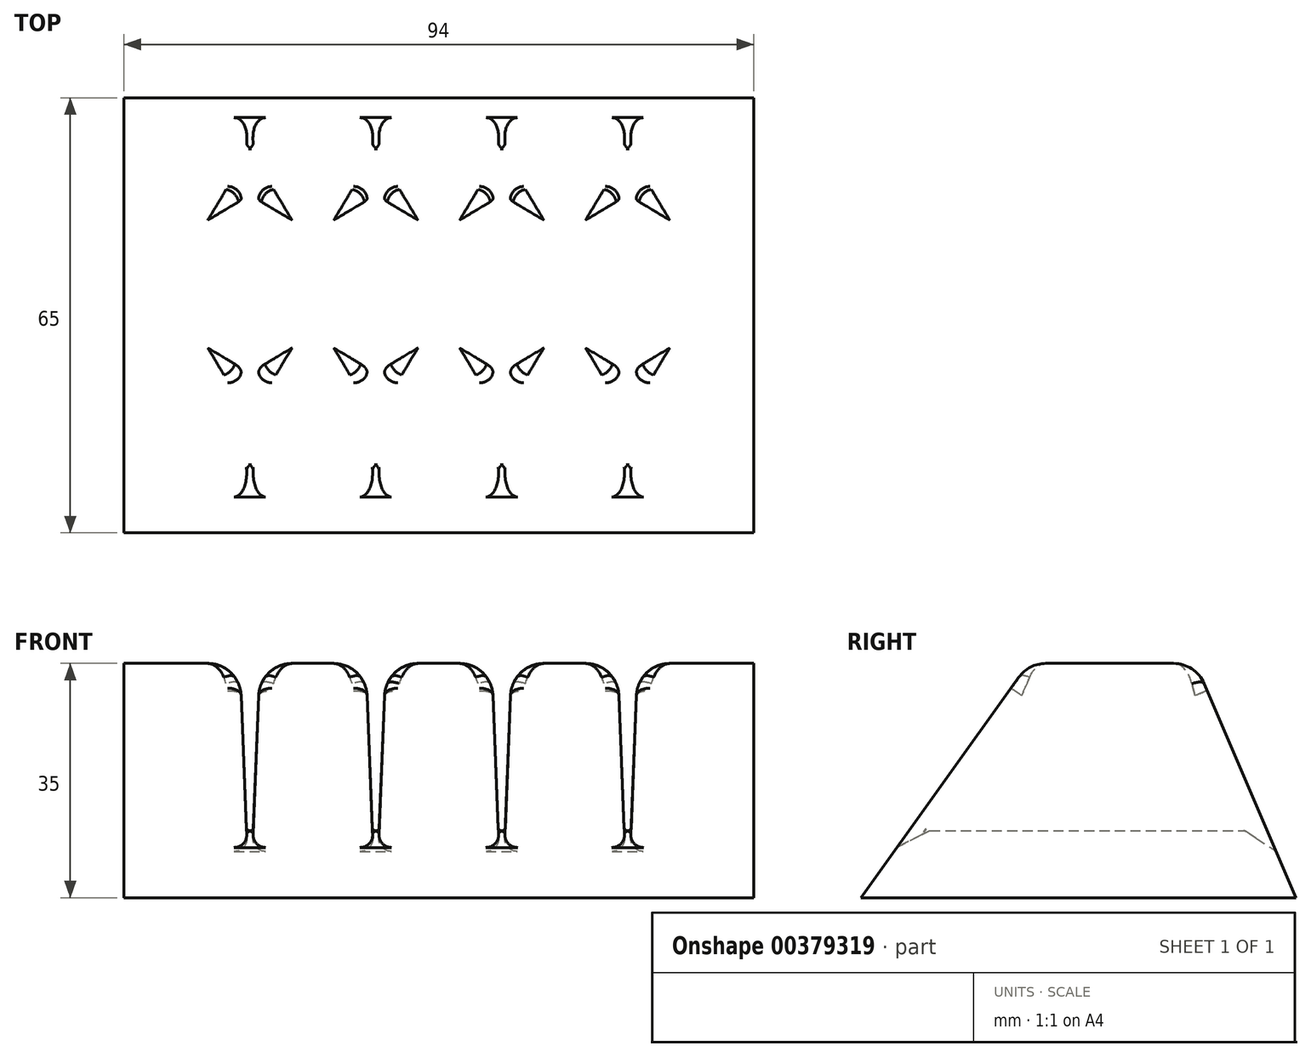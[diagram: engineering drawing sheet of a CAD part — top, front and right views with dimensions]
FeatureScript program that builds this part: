
annotation { "Feature Type Name" : "Feature", "Feature Type Description" : "" }
export const myFeature = defineFeature(function(context is Context, id is Id, definition is map)
    precondition{}
    {
        {
            var Q0;
            Q0=qCreatedBy(makeId("Front.planeOp"),FACE);
            var sketch = newSketch(context, id + "F0", { "sketchPlane" : qUnion([Q0])});
            skLineSegment(sketch, "E0", {"start": v(-114.12, 35) * mm, "end": v(-114.12, 0) * mm});
            skLineSegment(sketch, "E1", {"start": v(-114.12, 0) * mm, "end": v(-20.12, 0) * mm});
            skLineSegment(sketch, "E2", {"start": v(-20.12, 0) * mm, "end": v(-20.12, 35) * mm});
            skLineSegment(sketch, "E3", {"start": v(-56.22, 35) * mm, "end": v(-57.22, 10) * mm});
            skLineSegment(sketch, "E4", {"start": v(-57.22, 10) * mm, "end": v(-58.22, 10) * mm});
            skLineSegment(sketch, "E5", {"start": v(-58.22, 10) * mm, "end": v(-59.22, 35) * mm});
            skLineSegment(sketch, "E6", {"start": v(-75.02, 35) * mm, "end": v(-76.02, 10) * mm});
            skLineSegment(sketch, "E7", {"start": v(-76.02, 10) * mm, "end": v(-77.02, 10) * mm});
            skLineSegment(sketch, "E8", {"start": v(-77.02, 10) * mm, "end": v(-78.02, 35) * mm});
            skLineSegment(sketch, "E9", {"start": v(-93.82, 35) * mm, "end": v(-94.82, 10) * mm});
            skLineSegment(sketch, "E10", {"start": v(-94.82, 10) * mm, "end": v(-95.82, 10) * mm});
            skLineSegment(sketch, "E11", {"start": v(-95.82, 10) * mm, "end": v(-96.82, 35) * mm});
            skLineSegment(sketch, "E12", {"start": v(-38.42, 10) * mm, "end": v(-39.42, 10) * mm});
            skLineSegment(sketch, "E13", {"start": v(-39.42, 10) * mm, "end": v(-40.42, 35) * mm});
            skLineSegment(sketch, "E14", {"start": v(-37.42, 35) * mm, "end": v(-38.42, 10) * mm});
            skLineSegment(sketch, "E15", {"start": v(-114.12, 35) * mm, "end": v(-96.82, 35) * mm});
            skLineSegment(sketch, "E16", {"start": v(-93.82, 35) * mm, "end": v(-78.02, 35) * mm});
            skLineSegment(sketch, "E17", {"start": v(-75.02, 35) * mm, "end": v(-59.22, 35) * mm});
            skLineSegment(sketch, "E18", {"start": v(-56.22, 35) * mm, "end": v(-40.42, 35) * mm});
            skLineSegment(sketch, "E19", {"start": v(-37.42, 35) * mm, "end": v(-20.12, 35) * mm});
            skSolve(sketch);
        }
        {
            var Q0;
            Q0 = qSketchRegion(id + "F0", true);
            extrude(context, id + "F1", {"entities" : qUnion([Q0]), "depth" : 25 * mm});
        }
        {
            var Q0;
            Q0=makeQuery(id+"F1.opExtrude","CAP_FACE",FACE,{"disambiguationData":[OSD([sQuery(id+"F0.wireOp",EDGE,"E0"),sQuery(id+"F0.wireOp",EDGE,"E1"),sQuery(id+"F0.wireOp",EDGE,"E2"),sQuery(id+"F0.wireOp",EDGE,"E3"),sQuery(id+"F0.wireOp",EDGE,"E4"),sQuery(id+"F0.wireOp",EDGE,"E5"),sQuery(id+"F0.wireOp",EDGE,"E6"),sQuery(id+"F0.wireOp",EDGE,"E7"),sQuery(id+"F0.wireOp",EDGE,"E8"),sQuery(id+"F0.wireOp",EDGE,"E9"),sQuery(id+"F0.wireOp",EDGE,"E10"),sQuery(id+"F0.wireOp",EDGE,"E11"),sQuery(id+"F0.wireOp",EDGE,"E12"),sQuery(id+"F0.wireOp",EDGE,"E13"),sQuery(id+"F0.wireOp",EDGE,"E14"),sQuery(id+"F0.wireOp",EDGE,"E15"),sQuery(id+"F0.wireOp",EDGE,"E16"),sQuery(id+"F0.wireOp",EDGE,"E17"),sQuery(id+"F0.wireOp",EDGE,"E18"),sQuery(id+"F0.wireOp",EDGE,"E19")])],"isStart":false});
            extrude(context, id + "F2", {"entities" : qUnion([Q0]), "operationType" : NewBodyOperationType.ADD, "depth" : 25 * mm});
        }
        {
            var Q0;
            Q0=makeQuery(id+"F1.opExtrude","CAP_FACE",FACE,{"disambiguationData":[OSD([sQuery(id+"F0.wireOp",EDGE,"E0"),sQuery(id+"F0.wireOp",EDGE,"E1"),sQuery(id+"F0.wireOp",EDGE,"E2"),sQuery(id+"F0.wireOp",EDGE,"E3"),sQuery(id+"F0.wireOp",EDGE,"E4"),sQuery(id+"F0.wireOp",EDGE,"E5"),sQuery(id+"F0.wireOp",EDGE,"E6"),sQuery(id+"F0.wireOp",EDGE,"E7"),sQuery(id+"F0.wireOp",EDGE,"E8"),sQuery(id+"F0.wireOp",EDGE,"E9"),sQuery(id+"F0.wireOp",EDGE,"E10"),sQuery(id+"F0.wireOp",EDGE,"E11"),sQuery(id+"F0.wireOp",EDGE,"E12"),sQuery(id+"F0.wireOp",EDGE,"E13"),sQuery(id+"F0.wireOp",EDGE,"E14"),sQuery(id+"F0.wireOp",EDGE,"E15"),sQuery(id+"F0.wireOp",EDGE,"E16"),sQuery(id+"F0.wireOp",EDGE,"E17"),sQuery(id+"F0.wireOp",EDGE,"E18"),sQuery(id+"F0.wireOp",EDGE,"E19")])],"isStart":true});
            extrude(context, id + "F3", {"entities" : qUnion([Q0]), "operationType" : NewBodyOperationType.ADD, "depth" : 15 * mm});
        }
        {
            var Q0;
            {var subQ0=sQuery(id+"F0.wireOp",EDGE,"E0");Q0=makeQuery(id+"F3.boolean.opBoolean","MERGE",FACE,{"derivedFrom":[makeQuery(id+"F2.boolean.opBoolean","MERGE",FACE,{"derivedFrom":[makeQuery(id+"F1.opExtrude","SWEPT_FACE",FACE,{"disambiguationData":[OSD([subQ0])]}),makeQuery(id+"F2.opExtrude","SWEPT_FACE",FACE,{"disambiguationData":[OSD([subQ0])]})]}),makeQuery(id+"F3.opExtrude","SWEPT_FACE",FACE,{"disambiguationData":[OSD([subQ0])]})]});}
            var sketch = newSketch(context, id + "F4", { "sketchPlane" : qUnion([Q0])});
            skLineSegment(sketch, "E20", {"start": v(24.92, 35) * mm, "end": v(50, 0) * mm});
            skLineSegment(sketch, "E21", {"start": v(50, 0) * mm, "end": v(68.12, 0) * mm});
            skLineSegment(sketch, "E22", {"start": v(68.12, 0) * mm, "end": v(68.12, 46.5) * mm});
            skLineSegment(sketch, "E23", {"start": v(68.12, 46.5) * mm, "end": v(24.92, 35) * mm});
            skSolve(sketch);
        }
        {
            var Q0;
            Q0 = qSketchRegion(id + "F4", true);
            extrude(context, id + "F5", {"entities" : qUnion([Q0]), "operationType" : NewBodyOperationType.REMOVE, "endBound" : BoundingType.THROUGH_ALL, "oppositeDirection" : true, "depth" : 25 * mm});
        }
        {
            var Q0;
            {var subQ0=sQuery(id+"F0.wireOp",EDGE,"E0");Q0=makeQuery(id+"F3.boolean.opBoolean","MERGE",FACE,{"derivedFrom":[makeQuery(id+"F2.boolean.opBoolean","MERGE",FACE,{"derivedFrom":[makeQuery(id+"F1.opExtrude","SWEPT_FACE",FACE,{"disambiguationData":[OSD([subQ0])]}),makeQuery(id+"F2.opExtrude","SWEPT_FACE",FACE,{"disambiguationData":[OSD([subQ0])]})]}),makeQuery(id+"F3.opExtrude","SWEPT_FACE",FACE,{"disambiguationData":[OSD([subQ0])]})]});}
            var sketch = newSketch(context, id + "F6", { "sketchPlane" : qUnion([Q0])});
            skLineSegment(sketch, "E24", {"start": v(0, 35) * mm, "end": v(-15, 0) * mm});
            skLineSegment(sketch, "E25", {"start": v(-15, 0) * mm, "end": v(-37.92, 17) * mm});
            skLineSegment(sketch, "E26", {"start": v(-37.92, 17) * mm, "end": v(-15.46, 39.89) * mm});
            skLineSegment(sketch, "E27", {"start": v(-15.46, 39.89) * mm, "end": v(0, 35) * mm});
            skSolve(sketch);
        }
        {
            var Q0;
            Q0 = qSketchRegion(id + "F6", true);
            extrude(context, id + "F7", {"entities" : qUnion([Q0]), "operationType" : NewBodyOperationType.REMOVE, "endBound" : BoundingType.THROUGH_ALL, "oppositeDirection" : true, "depth" : 25 * mm});
        }
        {
            var Q0;
            {var subQ0=sQuery(id+"F0.wireOp",EDGE,"E14");Q0=makeQuery(id+"F7.boolean.opBoolean","INTERSECT",EDGE,{"derivedFrom":[makeQuery(id+"F3.boolean.opBoolean","MERGE",FACE,{"derivedFrom":[makeQuery(id+"F2.boolean.opBoolean","MERGE",FACE,{"derivedFrom":[makeQuery(id+"F1.opExtrude","SWEPT_FACE",FACE,{"disambiguationData":[OSD([subQ0])]}),makeQuery(id+"F2.opExtrude","SWEPT_FACE",FACE,{"disambiguationData":[OSD([subQ0])]})]}),makeQuery(id+"F3.opExtrude","SWEPT_FACE",FACE,{"disambiguationData":[OSD([subQ0])]})]}),makeQuery(id+"F7.opExtrude","SWEPT_FACE",FACE,{"disambiguationData":[OSD([sQuery(id+"F6.wireOp",EDGE,"E24")])]})]});}
            var Q1;
            {var subQ0=sQuery(id+"F0.wireOp",EDGE,"E13");Q1=makeQuery(id+"F7.boolean.opBoolean","INTERSECT",EDGE,{"derivedFrom":[makeQuery(id+"F3.boolean.opBoolean","MERGE",FACE,{"derivedFrom":[makeQuery(id+"F2.boolean.opBoolean","MERGE",FACE,{"derivedFrom":[makeQuery(id+"F1.opExtrude","SWEPT_FACE",FACE,{"disambiguationData":[OSD([subQ0])]}),makeQuery(id+"F2.opExtrude","SWEPT_FACE",FACE,{"disambiguationData":[OSD([subQ0])]})]}),makeQuery(id+"F3.opExtrude","SWEPT_FACE",FACE,{"disambiguationData":[OSD([subQ0])]})]}),makeQuery(id+"F7.opExtrude","SWEPT_FACE",FACE,{"disambiguationData":[OSD([sQuery(id+"F6.wireOp",EDGE,"E24")])]})]});}
            var Q2;
            {var subQ0=sQuery(id+"F0.wireOp",EDGE,"E3");Q2=makeQuery(id+"F7.boolean.opBoolean","INTERSECT",EDGE,{"derivedFrom":[makeQuery(id+"F3.boolean.opBoolean","MERGE",FACE,{"derivedFrom":[makeQuery(id+"F2.boolean.opBoolean","MERGE",FACE,{"derivedFrom":[makeQuery(id+"F1.opExtrude","SWEPT_FACE",FACE,{"disambiguationData":[OSD([subQ0])]}),makeQuery(id+"F2.opExtrude","SWEPT_FACE",FACE,{"disambiguationData":[OSD([subQ0])]})]}),makeQuery(id+"F3.opExtrude","SWEPT_FACE",FACE,{"disambiguationData":[OSD([subQ0])]})]}),makeQuery(id+"F7.opExtrude","SWEPT_FACE",FACE,{"disambiguationData":[OSD([sQuery(id+"F6.wireOp",EDGE,"E24")])]})]});}
            var Q3;
            {var subQ0=sQuery(id+"F0.wireOp",EDGE,"E5");Q3=makeQuery(id+"F7.boolean.opBoolean","INTERSECT",EDGE,{"derivedFrom":[makeQuery(id+"F3.boolean.opBoolean","MERGE",FACE,{"derivedFrom":[makeQuery(id+"F2.boolean.opBoolean","MERGE",FACE,{"derivedFrom":[makeQuery(id+"F1.opExtrude","SWEPT_FACE",FACE,{"disambiguationData":[OSD([subQ0])]}),makeQuery(id+"F2.opExtrude","SWEPT_FACE",FACE,{"disambiguationData":[OSD([subQ0])]})]}),makeQuery(id+"F3.opExtrude","SWEPT_FACE",FACE,{"disambiguationData":[OSD([subQ0])]})]}),makeQuery(id+"F7.opExtrude","SWEPT_FACE",FACE,{"disambiguationData":[OSD([sQuery(id+"F6.wireOp",EDGE,"E24")])]})]});}
            var Q4;
            {var subQ0=sQuery(id+"F0.wireOp",EDGE,"E6");Q4=makeQuery(id+"F7.boolean.opBoolean","INTERSECT",EDGE,{"derivedFrom":[makeQuery(id+"F3.boolean.opBoolean","MERGE",FACE,{"derivedFrom":[makeQuery(id+"F2.boolean.opBoolean","MERGE",FACE,{"derivedFrom":[makeQuery(id+"F1.opExtrude","SWEPT_FACE",FACE,{"disambiguationData":[OSD([subQ0])]}),makeQuery(id+"F2.opExtrude","SWEPT_FACE",FACE,{"disambiguationData":[OSD([subQ0])]})]}),makeQuery(id+"F3.opExtrude","SWEPT_FACE",FACE,{"disambiguationData":[OSD([subQ0])]})]}),makeQuery(id+"F7.opExtrude","SWEPT_FACE",FACE,{"disambiguationData":[OSD([sQuery(id+"F6.wireOp",EDGE,"E24")])]})]});}
            var Q5;
            {var subQ0=sQuery(id+"F0.wireOp",EDGE,"E8");Q5=makeQuery(id+"F7.boolean.opBoolean","INTERSECT",EDGE,{"derivedFrom":[makeQuery(id+"F3.boolean.opBoolean","MERGE",FACE,{"derivedFrom":[makeQuery(id+"F2.boolean.opBoolean","MERGE",FACE,{"derivedFrom":[makeQuery(id+"F1.opExtrude","SWEPT_FACE",FACE,{"disambiguationData":[OSD([subQ0])]}),makeQuery(id+"F2.opExtrude","SWEPT_FACE",FACE,{"disambiguationData":[OSD([subQ0])]})]}),makeQuery(id+"F3.opExtrude","SWEPT_FACE",FACE,{"disambiguationData":[OSD([subQ0])]})]}),makeQuery(id+"F7.opExtrude","SWEPT_FACE",FACE,{"disambiguationData":[OSD([sQuery(id+"F6.wireOp",EDGE,"E24")])]})]});}
            var Q6;
            {var subQ0=sQuery(id+"F0.wireOp",EDGE,"E9");Q6=makeQuery(id+"F7.boolean.opBoolean","INTERSECT",EDGE,{"derivedFrom":[makeQuery(id+"F3.boolean.opBoolean","MERGE",FACE,{"derivedFrom":[makeQuery(id+"F2.boolean.opBoolean","MERGE",FACE,{"derivedFrom":[makeQuery(id+"F1.opExtrude","SWEPT_FACE",FACE,{"disambiguationData":[OSD([subQ0])]}),makeQuery(id+"F2.opExtrude","SWEPT_FACE",FACE,{"disambiguationData":[OSD([subQ0])]})]}),makeQuery(id+"F3.opExtrude","SWEPT_FACE",FACE,{"disambiguationData":[OSD([subQ0])]})]}),makeQuery(id+"F7.opExtrude","SWEPT_FACE",FACE,{"disambiguationData":[OSD([sQuery(id+"F6.wireOp",EDGE,"E24")])]})]});}
            var Q7;
            {var subQ0=sQuery(id+"F0.wireOp",EDGE,"E11");Q7=makeQuery(id+"F7.boolean.opBoolean","INTERSECT",EDGE,{"derivedFrom":[makeQuery(id+"F3.boolean.opBoolean","MERGE",FACE,{"derivedFrom":[makeQuery(id+"F2.boolean.opBoolean","MERGE",FACE,{"derivedFrom":[makeQuery(id+"F1.opExtrude","SWEPT_FACE",FACE,{"disambiguationData":[OSD([subQ0])]}),makeQuery(id+"F2.opExtrude","SWEPT_FACE",FACE,{"disambiguationData":[OSD([subQ0])]})]}),makeQuery(id+"F3.opExtrude","SWEPT_FACE",FACE,{"disambiguationData":[OSD([subQ0])]})]}),makeQuery(id+"F7.opExtrude","SWEPT_FACE",FACE,{"disambiguationData":[OSD([sQuery(id+"F6.wireOp",EDGE,"E24")])]})]});}
            var Q8;
            {var subQ0=sQuery(id+"F0.wireOp",EDGE,"E11");Q8=makeQuery(id+"F5.boolean.opBoolean","INTERSECT",EDGE,{"derivedFrom":[makeQuery(id+"F3.boolean.opBoolean","MERGE",FACE,{"derivedFrom":[makeQuery(id+"F2.boolean.opBoolean","MERGE",FACE,{"derivedFrom":[makeQuery(id+"F1.opExtrude","SWEPT_FACE",FACE,{"disambiguationData":[OSD([subQ0])]}),makeQuery(id+"F2.opExtrude","SWEPT_FACE",FACE,{"disambiguationData":[OSD([subQ0])]})]}),makeQuery(id+"F3.opExtrude","SWEPT_FACE",FACE,{"disambiguationData":[OSD([subQ0])]})]}),makeQuery(id+"F5.opExtrude","SWEPT_FACE",FACE,{"disambiguationData":[OSD([sQuery(id+"F4.wireOp",EDGE,"E20")])]})]});}
            var Q9;
            {var subQ0=sQuery(id+"F0.wireOp",EDGE,"E9");Q9=makeQuery(id+"F5.boolean.opBoolean","INTERSECT",EDGE,{"derivedFrom":[makeQuery(id+"F3.boolean.opBoolean","MERGE",FACE,{"derivedFrom":[makeQuery(id+"F2.boolean.opBoolean","MERGE",FACE,{"derivedFrom":[makeQuery(id+"F1.opExtrude","SWEPT_FACE",FACE,{"disambiguationData":[OSD([subQ0])]}),makeQuery(id+"F2.opExtrude","SWEPT_FACE",FACE,{"disambiguationData":[OSD([subQ0])]})]}),makeQuery(id+"F3.opExtrude","SWEPT_FACE",FACE,{"disambiguationData":[OSD([subQ0])]})]}),makeQuery(id+"F5.opExtrude","SWEPT_FACE",FACE,{"disambiguationData":[OSD([sQuery(id+"F4.wireOp",EDGE,"E20")])]})]});}
            var Q10;
            {var subQ0=sQuery(id+"F0.wireOp",EDGE,"E8");Q10=makeQuery(id+"F5.boolean.opBoolean","INTERSECT",EDGE,{"derivedFrom":[makeQuery(id+"F3.boolean.opBoolean","MERGE",FACE,{"derivedFrom":[makeQuery(id+"F2.boolean.opBoolean","MERGE",FACE,{"derivedFrom":[makeQuery(id+"F1.opExtrude","SWEPT_FACE",FACE,{"disambiguationData":[OSD([subQ0])]}),makeQuery(id+"F2.opExtrude","SWEPT_FACE",FACE,{"disambiguationData":[OSD([subQ0])]})]}),makeQuery(id+"F3.opExtrude","SWEPT_FACE",FACE,{"disambiguationData":[OSD([subQ0])]})]}),makeQuery(id+"F5.opExtrude","SWEPT_FACE",FACE,{"disambiguationData":[OSD([sQuery(id+"F4.wireOp",EDGE,"E20")])]})]});}
            var Q11;
            {var subQ0=sQuery(id+"F0.wireOp",EDGE,"E6");Q11=makeQuery(id+"F5.boolean.opBoolean","INTERSECT",EDGE,{"derivedFrom":[makeQuery(id+"F3.boolean.opBoolean","MERGE",FACE,{"derivedFrom":[makeQuery(id+"F2.boolean.opBoolean","MERGE",FACE,{"derivedFrom":[makeQuery(id+"F1.opExtrude","SWEPT_FACE",FACE,{"disambiguationData":[OSD([subQ0])]}),makeQuery(id+"F2.opExtrude","SWEPT_FACE",FACE,{"disambiguationData":[OSD([subQ0])]})]}),makeQuery(id+"F3.opExtrude","SWEPT_FACE",FACE,{"disambiguationData":[OSD([subQ0])]})]}),makeQuery(id+"F5.opExtrude","SWEPT_FACE",FACE,{"disambiguationData":[OSD([sQuery(id+"F4.wireOp",EDGE,"E20")])]})]});}
            var Q12;
            {var subQ0=sQuery(id+"F0.wireOp",EDGE,"E5");Q12=makeQuery(id+"F5.boolean.opBoolean","INTERSECT",EDGE,{"derivedFrom":[makeQuery(id+"F3.boolean.opBoolean","MERGE",FACE,{"derivedFrom":[makeQuery(id+"F2.boolean.opBoolean","MERGE",FACE,{"derivedFrom":[makeQuery(id+"F1.opExtrude","SWEPT_FACE",FACE,{"disambiguationData":[OSD([subQ0])]}),makeQuery(id+"F2.opExtrude","SWEPT_FACE",FACE,{"disambiguationData":[OSD([subQ0])]})]}),makeQuery(id+"F3.opExtrude","SWEPT_FACE",FACE,{"disambiguationData":[OSD([subQ0])]})]}),makeQuery(id+"F5.opExtrude","SWEPT_FACE",FACE,{"disambiguationData":[OSD([sQuery(id+"F4.wireOp",EDGE,"E20")])]})]});}
            var Q13;
            {var subQ0=sQuery(id+"F0.wireOp",EDGE,"E3");Q13=makeQuery(id+"F5.boolean.opBoolean","INTERSECT",EDGE,{"derivedFrom":[makeQuery(id+"F3.boolean.opBoolean","MERGE",FACE,{"derivedFrom":[makeQuery(id+"F2.boolean.opBoolean","MERGE",FACE,{"derivedFrom":[makeQuery(id+"F1.opExtrude","SWEPT_FACE",FACE,{"disambiguationData":[OSD([subQ0])]}),makeQuery(id+"F2.opExtrude","SWEPT_FACE",FACE,{"disambiguationData":[OSD([subQ0])]})]}),makeQuery(id+"F3.opExtrude","SWEPT_FACE",FACE,{"disambiguationData":[OSD([subQ0])]})]}),makeQuery(id+"F5.opExtrude","SWEPT_FACE",FACE,{"disambiguationData":[OSD([sQuery(id+"F4.wireOp",EDGE,"E20")])]})]});}
            var Q14;
            {var subQ0=sQuery(id+"F0.wireOp",EDGE,"E13");Q14=makeQuery(id+"F5.boolean.opBoolean","INTERSECT",EDGE,{"derivedFrom":[makeQuery(id+"F3.boolean.opBoolean","MERGE",FACE,{"derivedFrom":[makeQuery(id+"F2.boolean.opBoolean","MERGE",FACE,{"derivedFrom":[makeQuery(id+"F1.opExtrude","SWEPT_FACE",FACE,{"disambiguationData":[OSD([subQ0])]}),makeQuery(id+"F2.opExtrude","SWEPT_FACE",FACE,{"disambiguationData":[OSD([subQ0])]})]}),makeQuery(id+"F3.opExtrude","SWEPT_FACE",FACE,{"disambiguationData":[OSD([subQ0])]})]}),makeQuery(id+"F5.opExtrude","SWEPT_FACE",FACE,{"disambiguationData":[OSD([sQuery(id+"F4.wireOp",EDGE,"E20")])]})]});}
            var Q15;
            {var subQ0=sQuery(id+"F0.wireOp",EDGE,"E14");Q15=makeQuery(id+"F5.boolean.opBoolean","INTERSECT",EDGE,{"derivedFrom":[makeQuery(id+"F3.boolean.opBoolean","MERGE",FACE,{"derivedFrom":[makeQuery(id+"F2.boolean.opBoolean","MERGE",FACE,{"derivedFrom":[makeQuery(id+"F1.opExtrude","SWEPT_FACE",FACE,{"disambiguationData":[OSD([subQ0])]}),makeQuery(id+"F2.opExtrude","SWEPT_FACE",FACE,{"disambiguationData":[OSD([subQ0])]})]}),makeQuery(id+"F3.opExtrude","SWEPT_FACE",FACE,{"disambiguationData":[OSD([subQ0])]})]}),makeQuery(id+"F5.opExtrude","SWEPT_FACE",FACE,{"disambiguationData":[OSD([sQuery(id+"F4.wireOp",EDGE,"E20")])]})]});}
            fillet(context, id + "F8", {"entities" : qUnion([Q0, Q1, Q2, Q3, Q4, Q5, Q6, Q7, Q8, Q9, Q10, Q11, Q12, Q13, Q14, Q15]), "radius" : 2 * mm, "tangentPropagation" : true, "allowEdgeOverflow" : false});
        }
        {
            var Q0;
            {var subQ0=sQuery(id+"F0.wireOp",EDGE,"E10");Q0=makeQuery(id+"F5.boolean.opBoolean","INTERSECT",EDGE,{"derivedFrom":[makeQuery(id+"F3.boolean.opBoolean","MERGE",FACE,{"derivedFrom":[makeQuery(id+"F2.boolean.opBoolean","MERGE",FACE,{"derivedFrom":[makeQuery(id+"F1.opExtrude","SWEPT_FACE",FACE,{"disambiguationData":[OSD([subQ0])]}),makeQuery(id+"F2.opExtrude","SWEPT_FACE",FACE,{"disambiguationData":[OSD([subQ0])]})]}),makeQuery(id+"F3.opExtrude","SWEPT_FACE",FACE,{"disambiguationData":[OSD([subQ0])]})]}),makeQuery(id+"F5.opExtrude","SWEPT_FACE",FACE,{"disambiguationData":[OSD([sQuery(id+"F4.wireOp",EDGE,"E20")])]})]});}
            var Q1;
            {var subQ0=sQuery(id+"F0.wireOp",EDGE,"E7");Q1=makeQuery(id+"F5.boolean.opBoolean","INTERSECT",EDGE,{"derivedFrom":[makeQuery(id+"F3.boolean.opBoolean","MERGE",FACE,{"derivedFrom":[makeQuery(id+"F2.boolean.opBoolean","MERGE",FACE,{"derivedFrom":[makeQuery(id+"F1.opExtrude","SWEPT_FACE",FACE,{"disambiguationData":[OSD([subQ0])]}),makeQuery(id+"F2.opExtrude","SWEPT_FACE",FACE,{"disambiguationData":[OSD([subQ0])]})]}),makeQuery(id+"F3.opExtrude","SWEPT_FACE",FACE,{"disambiguationData":[OSD([subQ0])]})]}),makeQuery(id+"F5.opExtrude","SWEPT_FACE",FACE,{"disambiguationData":[OSD([sQuery(id+"F4.wireOp",EDGE,"E20")])]})]});}
            var Q2;
            {var subQ0=sQuery(id+"F0.wireOp",EDGE,"E4");Q2=makeQuery(id+"F5.boolean.opBoolean","INTERSECT",EDGE,{"derivedFrom":[makeQuery(id+"F3.boolean.opBoolean","MERGE",FACE,{"derivedFrom":[makeQuery(id+"F2.boolean.opBoolean","MERGE",FACE,{"derivedFrom":[makeQuery(id+"F1.opExtrude","SWEPT_FACE",FACE,{"disambiguationData":[OSD([subQ0])]}),makeQuery(id+"F2.opExtrude","SWEPT_FACE",FACE,{"disambiguationData":[OSD([subQ0])]})]}),makeQuery(id+"F3.opExtrude","SWEPT_FACE",FACE,{"disambiguationData":[OSD([subQ0])]})]}),makeQuery(id+"F5.opExtrude","SWEPT_FACE",FACE,{"disambiguationData":[OSD([sQuery(id+"F4.wireOp",EDGE,"E20")])]})]});}
            var Q3;
            {var subQ0=sQuery(id+"F0.wireOp",EDGE,"E12");Q3=makeQuery(id+"F5.boolean.opBoolean","INTERSECT",EDGE,{"derivedFrom":[makeQuery(id+"F3.boolean.opBoolean","MERGE",FACE,{"derivedFrom":[makeQuery(id+"F2.boolean.opBoolean","MERGE",FACE,{"derivedFrom":[makeQuery(id+"F1.opExtrude","SWEPT_FACE",FACE,{"disambiguationData":[OSD([subQ0])]}),makeQuery(id+"F2.opExtrude","SWEPT_FACE",FACE,{"disambiguationData":[OSD([subQ0])]})]}),makeQuery(id+"F3.opExtrude","SWEPT_FACE",FACE,{"disambiguationData":[OSD([subQ0])]})]}),makeQuery(id+"F5.opExtrude","SWEPT_FACE",FACE,{"disambiguationData":[OSD([sQuery(id+"F4.wireOp",EDGE,"E20")])]})]});}
            chamfer(context, id + "F9", {"entities" : qUnion([Q0, Q1, Q2, Q3]), "width" : 6 * mm, "tangentPropagation" : true});
        }
        {
            var Q0;
            {var subQ0=sQuery(id+"F0.wireOp",EDGE,"E12");Q0=makeQuery(id+"F7.boolean.opBoolean","INTERSECT",EDGE,{"derivedFrom":[makeQuery(id+"F3.boolean.opBoolean","MERGE",FACE,{"derivedFrom":[makeQuery(id+"F2.boolean.opBoolean","MERGE",FACE,{"derivedFrom":[makeQuery(id+"F1.opExtrude","SWEPT_FACE",FACE,{"disambiguationData":[OSD([subQ0])]}),makeQuery(id+"F2.opExtrude","SWEPT_FACE",FACE,{"disambiguationData":[OSD([subQ0])]})]}),makeQuery(id+"F3.opExtrude","SWEPT_FACE",FACE,{"disambiguationData":[OSD([subQ0])]})]}),makeQuery(id+"F7.opExtrude","SWEPT_FACE",FACE,{"disambiguationData":[OSD([sQuery(id+"F6.wireOp",EDGE,"E24")])]})]});}
            var Q1;
            {var subQ0=sQuery(id+"F0.wireOp",EDGE,"E4");Q1=makeQuery(id+"F7.boolean.opBoolean","INTERSECT",EDGE,{"derivedFrom":[makeQuery(id+"F3.boolean.opBoolean","MERGE",FACE,{"derivedFrom":[makeQuery(id+"F2.boolean.opBoolean","MERGE",FACE,{"derivedFrom":[makeQuery(id+"F1.opExtrude","SWEPT_FACE",FACE,{"disambiguationData":[OSD([subQ0])]}),makeQuery(id+"F2.opExtrude","SWEPT_FACE",FACE,{"disambiguationData":[OSD([subQ0])]})]}),makeQuery(id+"F3.opExtrude","SWEPT_FACE",FACE,{"disambiguationData":[OSD([subQ0])]})]}),makeQuery(id+"F7.opExtrude","SWEPT_FACE",FACE,{"disambiguationData":[OSD([sQuery(id+"F6.wireOp",EDGE,"E24")])]})]});}
            var Q2;
            {var subQ0=sQuery(id+"F0.wireOp",EDGE,"E7");Q2=makeQuery(id+"F7.boolean.opBoolean","INTERSECT",EDGE,{"derivedFrom":[makeQuery(id+"F3.boolean.opBoolean","MERGE",FACE,{"derivedFrom":[makeQuery(id+"F2.boolean.opBoolean","MERGE",FACE,{"derivedFrom":[makeQuery(id+"F1.opExtrude","SWEPT_FACE",FACE,{"disambiguationData":[OSD([subQ0])]}),makeQuery(id+"F2.opExtrude","SWEPT_FACE",FACE,{"disambiguationData":[OSD([subQ0])]})]}),makeQuery(id+"F3.opExtrude","SWEPT_FACE",FACE,{"disambiguationData":[OSD([subQ0])]})]}),makeQuery(id+"F7.opExtrude","SWEPT_FACE",FACE,{"disambiguationData":[OSD([sQuery(id+"F6.wireOp",EDGE,"E24")])]})]});}
            var Q3;
            {var subQ0=sQuery(id+"F0.wireOp",EDGE,"E10");Q3=makeQuery(id+"F7.boolean.opBoolean","INTERSECT",EDGE,{"derivedFrom":[makeQuery(id+"F3.boolean.opBoolean","MERGE",FACE,{"derivedFrom":[makeQuery(id+"F2.boolean.opBoolean","MERGE",FACE,{"derivedFrom":[makeQuery(id+"F1.opExtrude","SWEPT_FACE",FACE,{"disambiguationData":[OSD([subQ0])]}),makeQuery(id+"F2.opExtrude","SWEPT_FACE",FACE,{"disambiguationData":[OSD([subQ0])]})]}),makeQuery(id+"F3.opExtrude","SWEPT_FACE",FACE,{"disambiguationData":[OSD([subQ0])]})]}),makeQuery(id+"F7.opExtrude","SWEPT_FACE",FACE,{"disambiguationData":[OSD([sQuery(id+"F6.wireOp",EDGE,"E24")])]})]});}
            chamfer(context, id + "F10", {"entities" : qUnion([Q0, Q1, Q2, Q3]), "width" : 5.1 * mm, "tangentPropagation" : true});
        }
        {
            var Q0;
            {var subQ0=sQuery(id+"F0.wireOp",EDGE,"E10");Q0=makeQuery(id+"F3.boolean.opBoolean","MERGE",FACE,{"derivedFrom":[makeQuery(id+"F2.boolean.opBoolean","MERGE",FACE,{"derivedFrom":[makeQuery(id+"F1.opExtrude","SWEPT_FACE",FACE,{"disambiguationData":[OSD([subQ0])]}),makeQuery(id+"F2.opExtrude","SWEPT_FACE",FACE,{"disambiguationData":[OSD([subQ0])]})]}),makeQuery(id+"F3.opExtrude","SWEPT_FACE",FACE,{"disambiguationData":[OSD([subQ0])]})]});}
            var Q1;
            {var subQ0=sQuery(id+"F0.wireOp",EDGE,"E7");Q1=makeQuery(id+"F3.boolean.opBoolean","MERGE",FACE,{"derivedFrom":[makeQuery(id+"F2.boolean.opBoolean","MERGE",FACE,{"derivedFrom":[makeQuery(id+"F1.opExtrude","SWEPT_FACE",FACE,{"disambiguationData":[OSD([subQ0])]}),makeQuery(id+"F2.opExtrude","SWEPT_FACE",FACE,{"disambiguationData":[OSD([subQ0])]})]}),makeQuery(id+"F3.opExtrude","SWEPT_FACE",FACE,{"disambiguationData":[OSD([subQ0])]})]});}
            var Q2;
            {var subQ0=sQuery(id+"F0.wireOp",EDGE,"E4");Q2=makeQuery(id+"F3.boolean.opBoolean","MERGE",FACE,{"derivedFrom":[makeQuery(id+"F2.boolean.opBoolean","MERGE",FACE,{"derivedFrom":[makeQuery(id+"F1.opExtrude","SWEPT_FACE",FACE,{"disambiguationData":[OSD([subQ0])]}),makeQuery(id+"F2.opExtrude","SWEPT_FACE",FACE,{"disambiguationData":[OSD([subQ0])]})]}),makeQuery(id+"F3.opExtrude","SWEPT_FACE",FACE,{"disambiguationData":[OSD([subQ0])]})]});}
            var Q3;
            {var subQ0=sQuery(id+"F0.wireOp",EDGE,"E12");Q3=makeQuery(id+"F3.boolean.opBoolean","MERGE",FACE,{"derivedFrom":[makeQuery(id+"F2.boolean.opBoolean","MERGE",FACE,{"derivedFrom":[makeQuery(id+"F1.opExtrude","SWEPT_FACE",FACE,{"disambiguationData":[OSD([subQ0])]}),makeQuery(id+"F2.opExtrude","SWEPT_FACE",FACE,{"disambiguationData":[OSD([subQ0])]})]}),makeQuery(id+"F3.opExtrude","SWEPT_FACE",FACE,{"disambiguationData":[OSD([subQ0])]})]});}
            fillet(context, id + "F11", {"entities" : qUnion([Q0, Q1, Q2, Q3]), "radius" : 0.5 * mm, "tangentPropagation" : true, "allowEdgeOverflow" : false});
        }
        {
            var Q0;
            {var subQ0=sQuery(id+"F0.wireOp",EDGE,"E16");var subQ1=sQuery(id+"F0.wireOp",EDGE,"E8");Q0=makeQuery(id+"F3.boolean.opBoolean","MERGE",EDGE,{"derivedFrom":[makeQuery(id+"F2.boolean.opBoolean","MERGE",EDGE,{"derivedFrom":[makeQuery(id+"F1.opExtrude","SWEPT_EDGE",EDGE,{"disambiguationData":[OSD([subQ1,subQ0])]}),makeQuery(id+"F2.opExtrude","SWEPT_EDGE",EDGE,{"disambiguationData":[OSD([subQ1,subQ0])]})]}),makeQuery(id+"F3.opExtrude","SWEPT_EDGE",EDGE,{"disambiguationData":[OSD([subQ1,subQ0])]})]});}
            var Q1;
            {var subQ0=sQuery(id+"F0.wireOp",EDGE,"E15");var subQ1=sQuery(id+"F0.wireOp",EDGE,"E11");Q1=makeQuery(id+"F3.boolean.opBoolean","MERGE",EDGE,{"derivedFrom":[makeQuery(id+"F2.boolean.opBoolean","MERGE",EDGE,{"derivedFrom":[makeQuery(id+"F1.opExtrude","SWEPT_EDGE",EDGE,{"disambiguationData":[OSD([subQ1,subQ0])]}),makeQuery(id+"F2.opExtrude","SWEPT_EDGE",EDGE,{"disambiguationData":[OSD([subQ1,subQ0])]})]}),makeQuery(id+"F3.opExtrude","SWEPT_EDGE",EDGE,{"disambiguationData":[OSD([subQ1,subQ0])]})]});}
            var Q2;
            {var subQ0=sQuery(id+"F0.wireOp",EDGE,"E17");var subQ1=sQuery(id+"F0.wireOp",EDGE,"E6");Q2=makeQuery(id+"F3.boolean.opBoolean","MERGE",EDGE,{"derivedFrom":[makeQuery(id+"F2.boolean.opBoolean","MERGE",EDGE,{"derivedFrom":[makeQuery(id+"F1.opExtrude","SWEPT_EDGE",EDGE,{"disambiguationData":[OSD([subQ1,subQ0])]}),makeQuery(id+"F2.opExtrude","SWEPT_EDGE",EDGE,{"disambiguationData":[OSD([subQ1,subQ0])]})]}),makeQuery(id+"F3.opExtrude","SWEPT_EDGE",EDGE,{"disambiguationData":[OSD([subQ1,subQ0])]})]});}
            var Q3;
            {var subQ0=sQuery(id+"F0.wireOp",EDGE,"E18");var subQ1=sQuery(id+"F0.wireOp",EDGE,"E3");Q3=makeQuery(id+"F3.boolean.opBoolean","MERGE",EDGE,{"derivedFrom":[makeQuery(id+"F2.boolean.opBoolean","MERGE",EDGE,{"derivedFrom":[makeQuery(id+"F1.opExtrude","SWEPT_EDGE",EDGE,{"disambiguationData":[OSD([subQ1,subQ0])]}),makeQuery(id+"F2.opExtrude","SWEPT_EDGE",EDGE,{"disambiguationData":[OSD([subQ1,subQ0])]})]}),makeQuery(id+"F3.opExtrude","SWEPT_EDGE",EDGE,{"disambiguationData":[OSD([subQ1,subQ0])]})]});}
            var Q4;
            {var subQ0=sQuery(id+"F0.wireOp",EDGE,"E19");var subQ1=sQuery(id+"F0.wireOp",EDGE,"E14");Q4=makeQuery(id+"F3.boolean.opBoolean","MERGE",EDGE,{"derivedFrom":[makeQuery(id+"F2.boolean.opBoolean","MERGE",EDGE,{"derivedFrom":[makeQuery(id+"F1.opExtrude","SWEPT_EDGE",EDGE,{"disambiguationData":[OSD([subQ1,subQ0])]}),makeQuery(id+"F2.opExtrude","SWEPT_EDGE",EDGE,{"disambiguationData":[OSD([subQ1,subQ0])]})]}),makeQuery(id+"F3.opExtrude","SWEPT_EDGE",EDGE,{"disambiguationData":[OSD([subQ1,subQ0])]})]});}
            fillet(context, id + "F12", {"entities" : qUnion([Q0, Q1, Q2, Q3, Q4]), "radius" : 5 * mm, "tangentPropagation" : true, "allowEdgeOverflow" : false});
        }
    });
